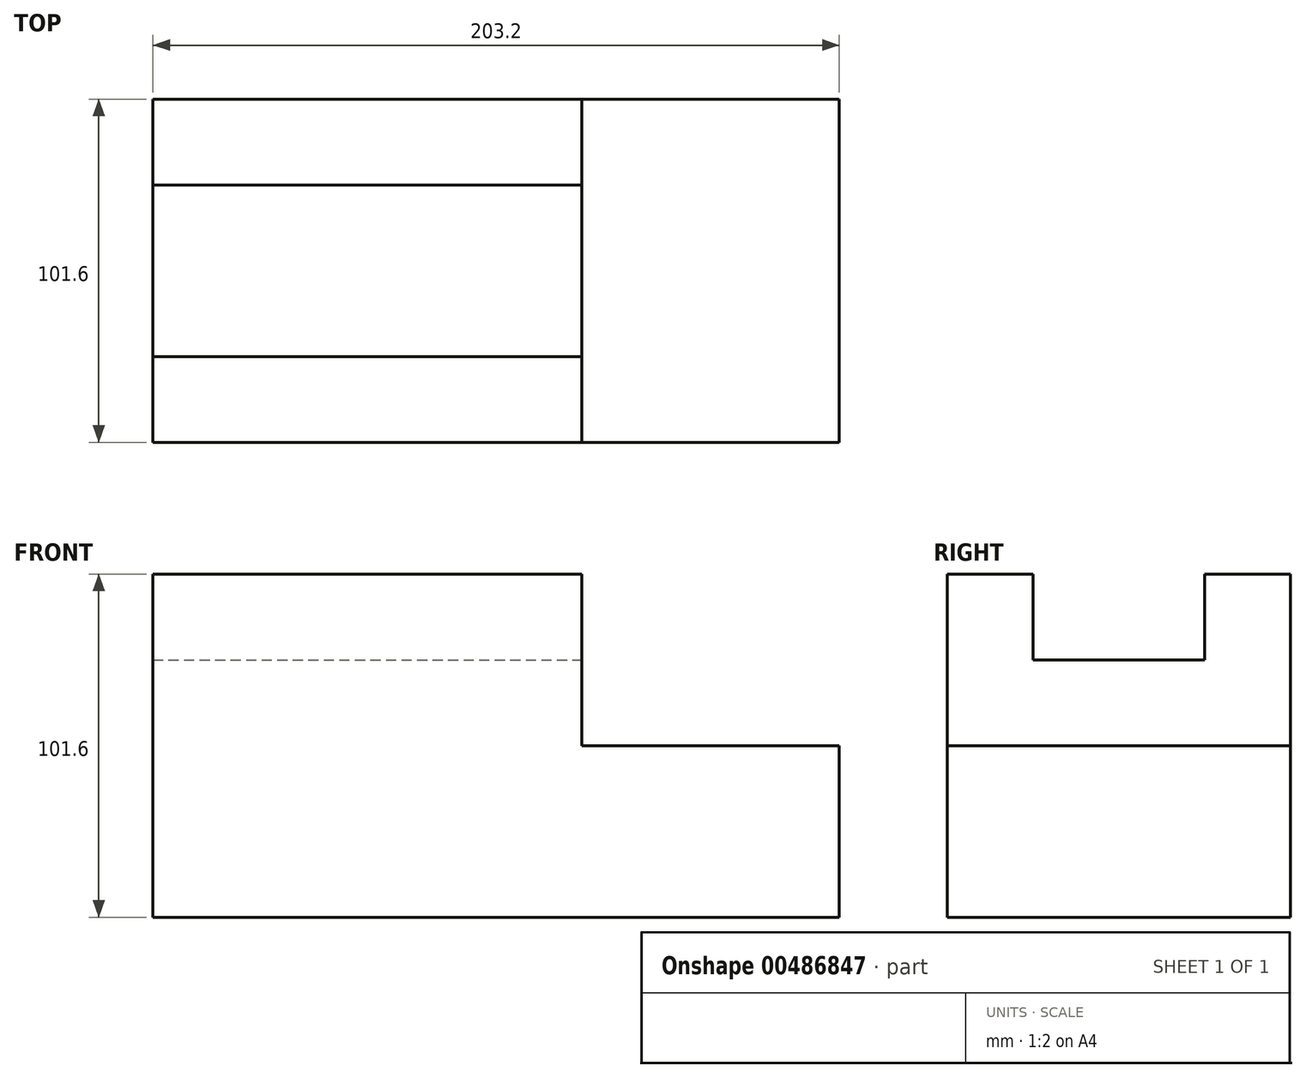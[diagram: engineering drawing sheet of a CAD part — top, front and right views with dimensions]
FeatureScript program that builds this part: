
annotation { "Feature Type Name" : "Feature", "Feature Type Description" : "" }
export const myFeature = defineFeature(function(context is Context, id is Id, definition is map)
    precondition{}
    {
        {
            var Q0;
            Q0=qCreatedBy(makeId("Front.planeOp"),FACE);
            var sketch = newSketch(context, id + "F0", { "sketchPlane" : qUnion([Q0])});
            skLineSegment(sketch, "E0.bottom", {"start": v(0, 0) * mm, "end": v(-203.2, 0) * mm});
            skLineSegment(sketch, "E0.top", {"start": v(-76.2, 101.6) * mm, "end": v(-203.2, 101.6) * mm});
            skLineSegment(sketch, "E0.left", {"start": v(0, 0) * mm, "end": v(0, 50.8) * mm});
            skLineSegment(sketch, "E0.right", {"start": v(-203.2, 0) * mm, "end": v(-203.2, 101.6) * mm});
            skLineSegment(sketch, "E1.top", {"start": v(0, 50.8) * mm, "end": v(-76.2, 50.8) * mm});
            skLineSegment(sketch, "E1.right", {"start": v(-76.2, 101.6) * mm, "end": v(-76.2, 50.8) * mm});
            skSolve(sketch);
        }
        {
            var Q0;
            Q0 = qSketchRegion(id + "F0", true);
            extrude(context, id + "F1", {"entities" : qUnion([Q0]), "depth" : 101.6 * mm});
        }
        {
            var Q0;
            Q0=makeQuery(id+"F1.opExtrude","SWEPT_FACE",FACE,{"disambiguationData":[OSD([sQuery(id+"F0.wireOp",EDGE,"E0.top")])]});
            var sketch = newSketch(context, id + "F2", { "sketchPlane" : qUnion([Q0])});
            skLineSegment(sketch, "E2.top", {"start": v(-203.2, -25.4) * mm, "end": v(-76.2, -25.4) * mm});
            skLineSegment(sketch, "E3.bottom", {"start": v(-203.2, -25.4) * mm, "end": v(-68.58, -25.4) * mm});
            skLineSegment(sketch, "E3.top", {"start": v(-203.2, -76.2) * mm, "end": v(-68.58, -76.2) * mm});
            skLineSegment(sketch, "E3.left", {"start": v(-203.2, -25.4) * mm, "end": v(-203.2, -76.2) * mm});
            skLineSegment(sketch, "E3.right", {"start": v(-68.58, -25.4) * mm, "end": v(-68.58, -76.2) * mm});
            skPoint(sketch, "E2.left.start.orphan", {"position": v(-203.2, 0) * mm});
            skSolve(sketch);
        }
        {
            var Q0;
            Q0 = qSketchRegion(id + "F2", true);
            extrude(context, id + "F3", {"entities" : qUnion([Q0]), "operationType" : NewBodyOperationType.REMOVE, "oppositeDirection" : true, "depth" : 25.4 * mm});
        }
    });
